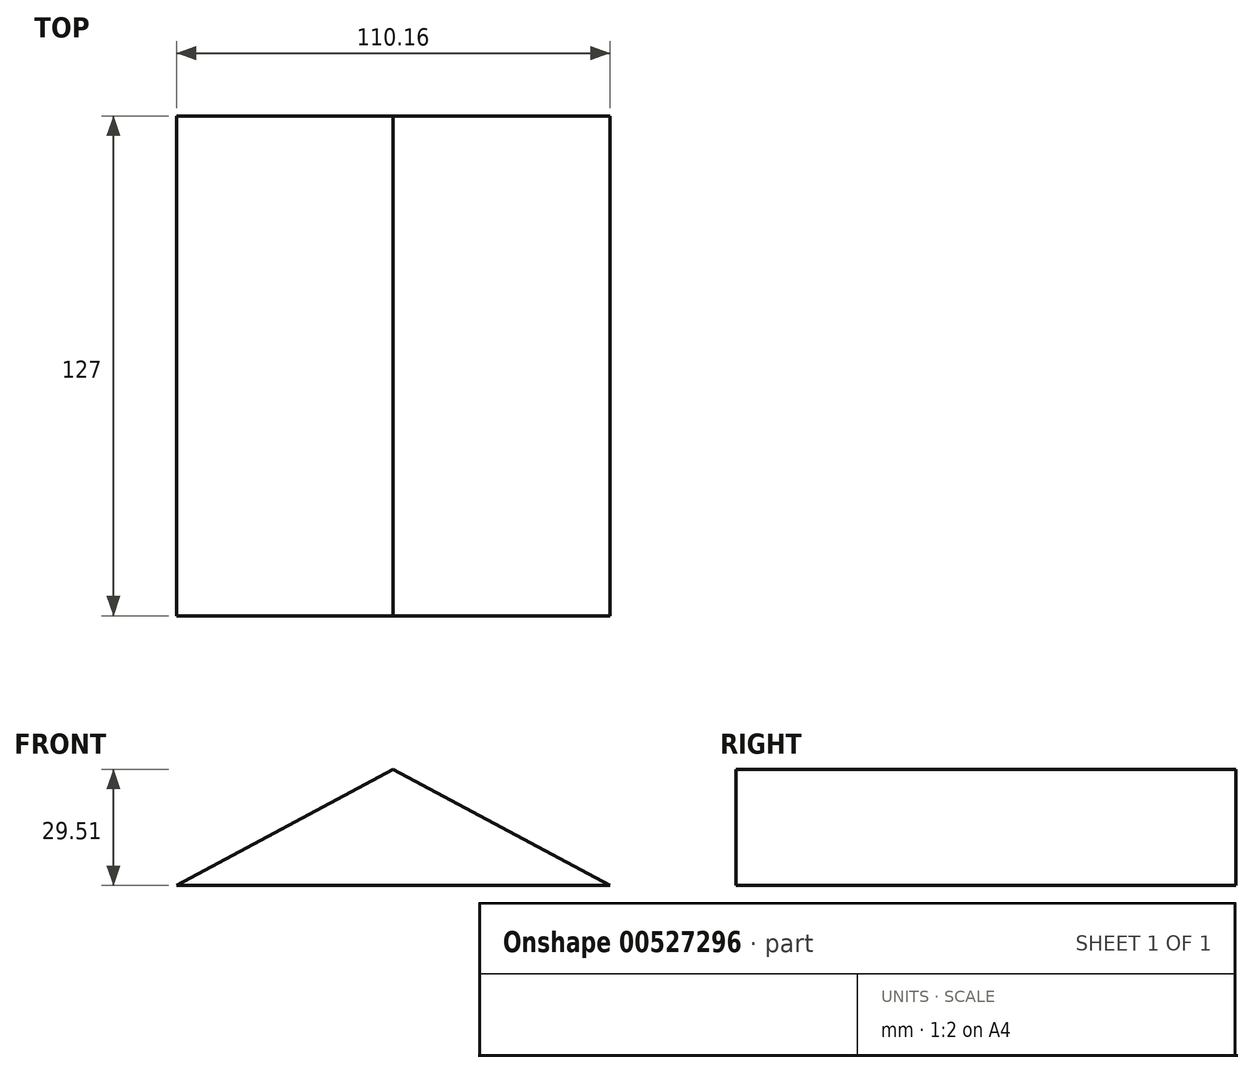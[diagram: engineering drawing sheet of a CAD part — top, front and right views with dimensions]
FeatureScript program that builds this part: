
annotation { "Feature Type Name" : "Feature", "Feature Type Description" : "" }
export const myFeature = defineFeature(function(context is Context, id is Id, definition is map)
    precondition{}
    {
        {
            var Q0;
            Q0=qCreatedBy(makeId("Front.planeOp"),FACE);
            var sketch = newSketch(context, id + "F0", { "sketchPlane" : qUnion([Q0])});
            skLineSegment(sketch, "E0", {"start": v(-65.31, 0) * mm, "end": v(-10.23, 0) * mm});
            skLineSegment(sketch, "E1", {"start": v(-10.23, 0) * mm, "end": v(44.85, 0) * mm});
            skLineSegment(sketch, "E2", {"start": v(-10.23, 0) * mm, "end": v(-10.23, 29.5) * mm});
            skLineSegment(sketch, "E3", {"start": v(-10.23, 29.5) * mm, "end": v(44.85, 0) * mm});
            skLineSegment(sketch, "E4", {"start": v(-10.23, 29.5) * mm, "end": v(-65.31, 0) * mm});
            skSolve(sketch);
        }
        {
            var Q0;
            Q0 = qSketchRegion(id + "F0", true);
            extrude(context, id + "F1", {"entities" : qUnion([Q0]), "depth" : 25.4 * mm, "offsetDistance" : 25.4 * mm});
        }
        {
            var Q0;
            Q0=makeQuery(id+"F1.opExtrude","CAP_FACE",FACE,{"disambiguationData":[OSD([sQuery(id+"F0.wireOp",EDGE,"E0"),sQuery(id+"F0.wireOp",EDGE,"E1"),sQuery(id+"F0.wireOp",EDGE,"E3"),sQuery(id+"F0.wireOp",EDGE,"E4")])],"isStart":false});
            extrude(context, id + "F2", {"entities" : qUnion([Q0]), "operationType" : NewBodyOperationType.ADD, "depth" : 25.4 * mm, "offsetDistance" : 25.4 * mm});
        }
        {
            var Q0;
            Q0=makeQuery(id+"F2.opExtrude","CAP_FACE",FACE,{"disambiguationData":[OSD([sQuery(id+"F0.wireOp",EDGE,"E0"),sQuery(id+"F0.wireOp",EDGE,"E1"),sQuery(id+"F0.wireOp",EDGE,"E3"),sQuery(id+"F0.wireOp",EDGE,"E4")])],"isStart":false});
            extrude(context, id + "F3", {"entities" : qUnion([Q0]), "operationType" : NewBodyOperationType.ADD, "depth" : 76.2 * mm, "offsetDistance" : 25.4 * mm});
        }
    });
